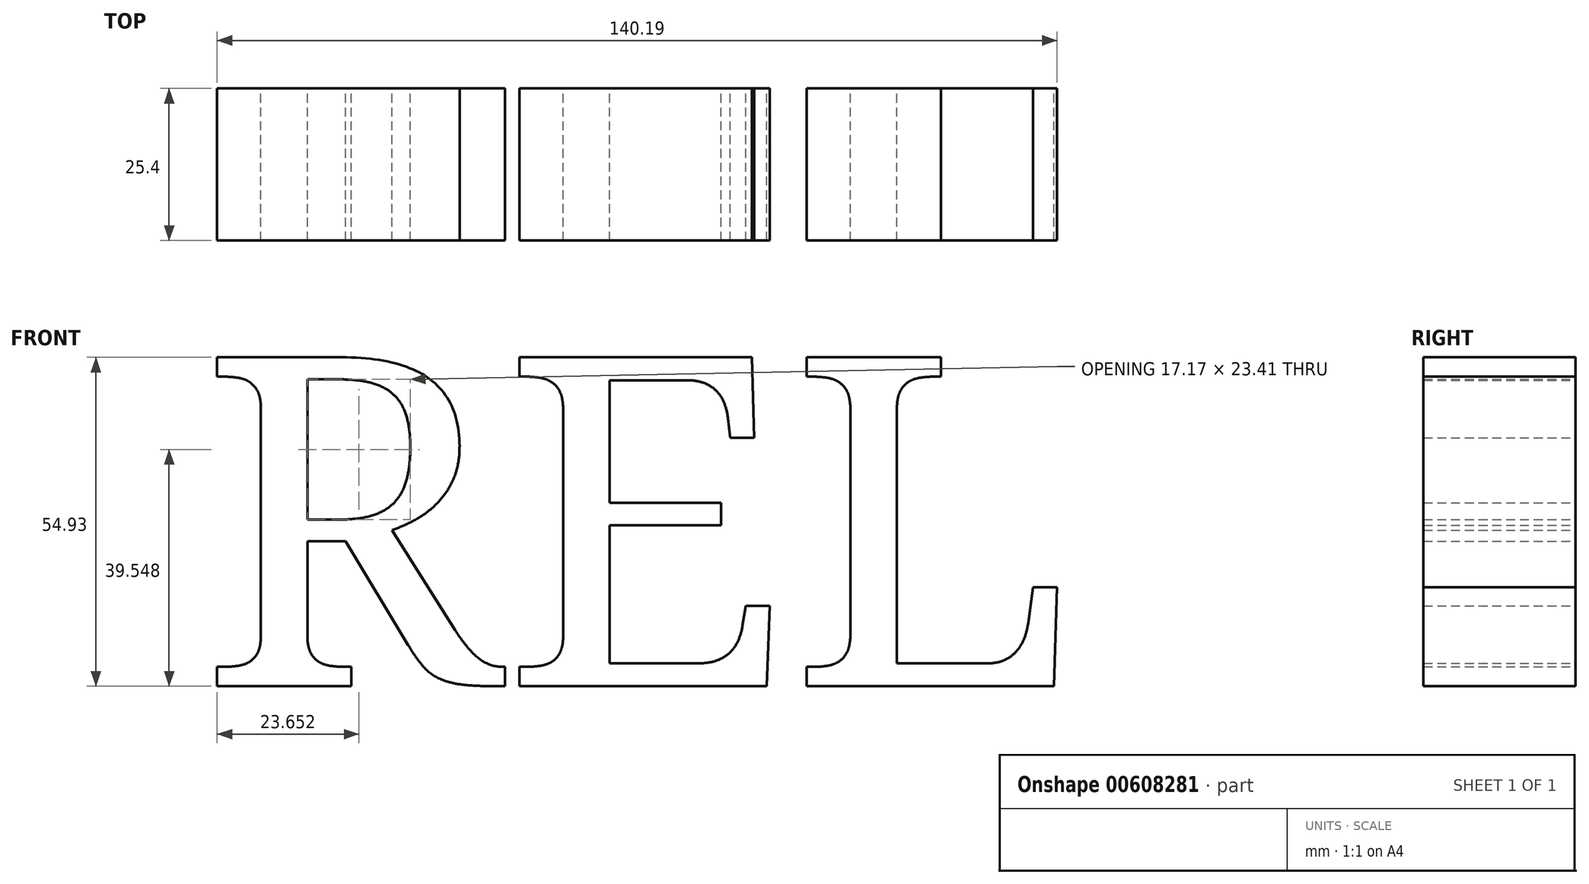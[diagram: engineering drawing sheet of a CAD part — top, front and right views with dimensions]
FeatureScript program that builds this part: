
annotation { "Feature Type Name" : "Feature", "Feature Type Description" : "" }
export const myFeature = defineFeature(function(context is Context, id is Id, definition is map)
    precondition{}
    {
        {
            var Q0;
            Q0=qCreatedBy(makeId("Front.planeOp"),FACE);
            var sketch = newSketch(context, id + "F0", { "sketchPlane" : qUnion([Q0])});
            skText(sketch, "E0", { "text": "REL", "fontName": "NotoSerif-Regular.ttf"});
            const initialGuessF0  = {"E0": [-0.07404, 0, 1, 0, 0.0554]};
            skSetInitialGuess(sketch, initialGuessF0);
            skSolve(sketch);
        }
        {
            var Q0;
            Q0 = qSketchRegion(id + "F0", true);
            extrude(context, id + "F1", {"entities" : qUnion([Q0]), "depth" : 25.4 * mm, "offsetDistance" : 25.4 * mm});
        }
    });
